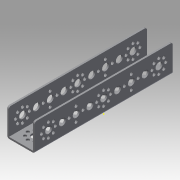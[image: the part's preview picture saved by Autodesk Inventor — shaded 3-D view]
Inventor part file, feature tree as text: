
AUTODESK INVENTOR PART (.ipt)
format: ipt  version: 2016 (Build 200138000, 138)  size: 348,672 bytes
history: native  units: in
note: dims shown in document units (in); Inventor stores cm internally (conversion verified against a paired STEP export)
features: other x1, imported_body x1, move_body x1, sketch x1
ambient origin geometry x8: Origin, YZ Plane, XZ Plane, XY Plane, X Axis, Y Axis, Z Axis, Center Point
bodies: Body1 (feature_tree)
feature tree (4):
  other  "CHANNEL_160_2011"
  imported_body  "Base1"
  move_body  "Move Body1"
  sketch  "Sketch3"  dims[d0=0.0in d1=0.0in d2=2.5197in]
